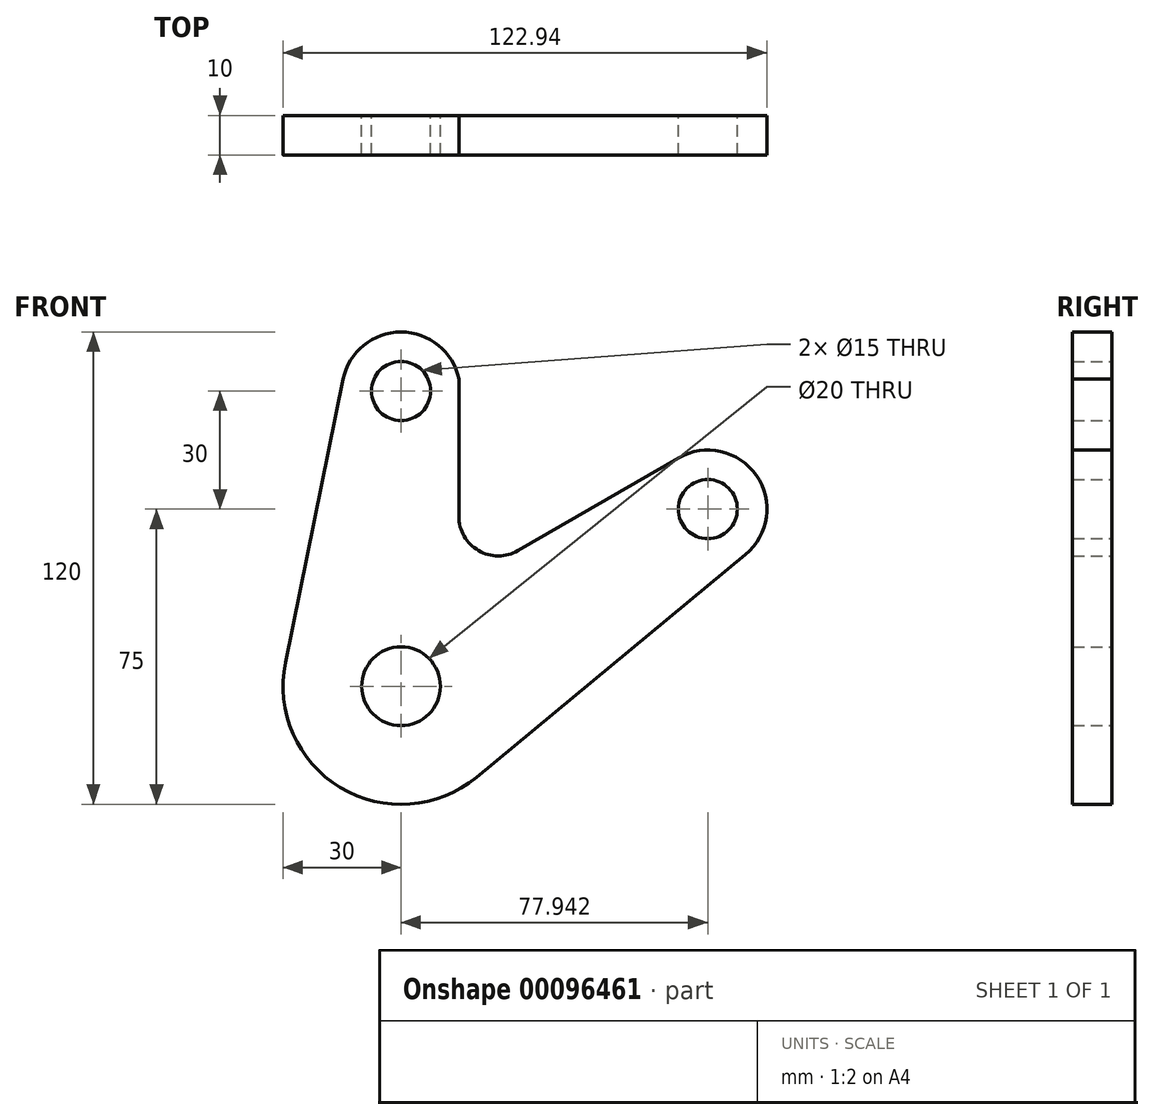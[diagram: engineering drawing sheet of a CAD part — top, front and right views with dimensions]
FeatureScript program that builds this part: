
annotation { "Feature Type Name" : "Feature", "Feature Type Description" : "" }
export const myFeature = defineFeature(function(context is Context, id is Id, definition is map)
    precondition{}
    {
        {
            var Q0;
            Q0=qCreatedBy(makeId("Front.planeOp"),FACE);
            var sketch = newSketch(context, id + "F0", { "sketchPlane" : qUnion([Q0])});
            skCircle(sketch, "E0", {"center": v(0, 0) * mm, "radius": 10 * mm});
            skLineSegment(sketch, "E1", {"start": v(0, 0) * mm, "end": v(0, 75) * mm, "construction": true});
            skLineSegment(sketch, "E2", {"start": v(0, 0) * mm, "end": v(77.94, 45) * mm, "construction": true});
            skCircle(sketch, "E3", {"center": v(0, 75) * mm, "radius": 7.5 * mm});
            skCircle(sketch, "E4", {"center": v(77.94, 45) * mm, "radius": 7.5 * mm});
            skLineSegment(sketch, "E5", {"start": v(19.12, -23.12) * mm, "end": v(87.5, 33.44) * mm});
            skLineSegment(sketch, "E6", {"start": v(29.7, 34.47) * mm, "end": v(70.44, 58) * mm});
            skPoint(sketch, "E7.visualSharp", {"position": v(15, 25.98) * mm});
            skArc(sketch, "E7.filletArc", {"start": v(14.7, 43.13) * mm, "mid": v(19.7, 34.47) * mm, "end": v(29.7, 34.47) * mm});
            skArc(sketch, "E8", {"start": v(19.12, -23.12) * mm, "mid": v(-15.44, -25.72) * mm, "end": v(-29.4, 6) * mm});
            skArc(sketch, "E9", {"start": v(87.5, 33.44) * mm, "mid": v(90.26, 53.56) * mm, "end": v(70.44, 58) * mm});
            skArc(sketch, "E10", {"start": v(14.7, 78) * mm, "mid": v(0, 90) * mm, "end": v(-14.7, 78) * mm});
            skLineSegment(sketch, "E11", {"start": v(14.7, 43.13) * mm, "end": v(14.7, 78) * mm});
            skLineSegment(sketch, "E12", {"start": v(-14.7, 78) * mm, "end": v(-29.4, 6) * mm});
            skSolve(sketch);
        }
        {
            var Q0;
            Q0 = qSketchRegion(id + "F0", true);
            extrude(context, id + "F1", {"entities" : qUnion([Q0]), "depth" : 10 * mm});
        }
    });
